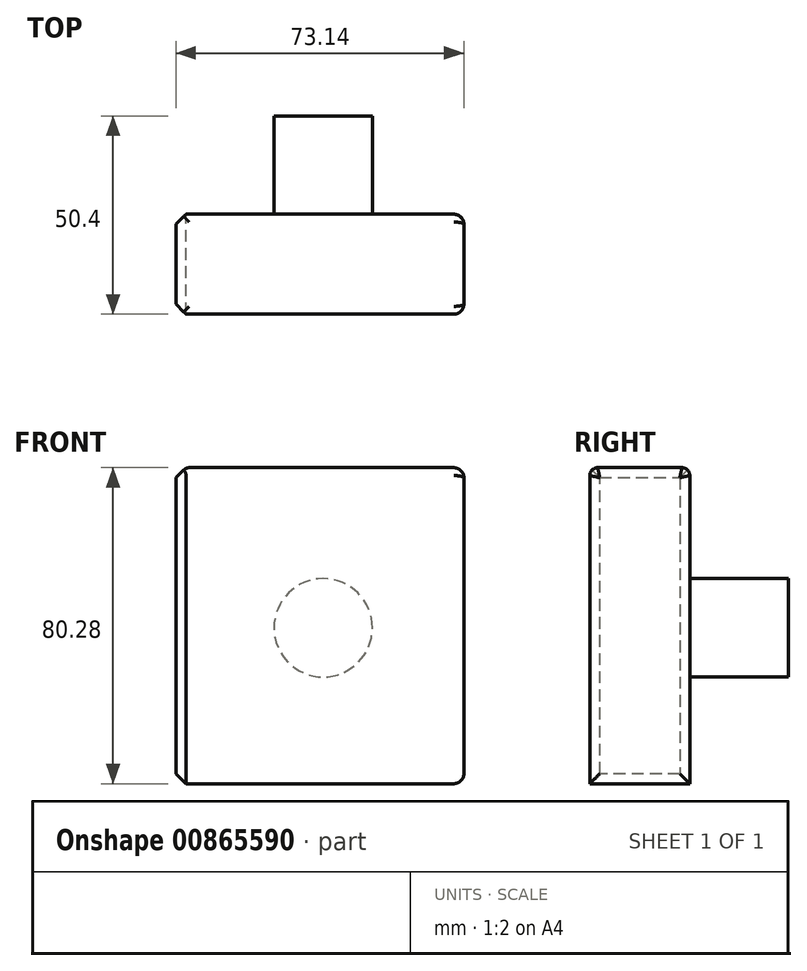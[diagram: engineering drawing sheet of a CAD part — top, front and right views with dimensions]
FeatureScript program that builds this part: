
annotation { "Feature Type Name" : "Feature", "Feature Type Description" : "" }
export const myFeature = defineFeature(function(context is Context, id is Id, definition is map)
    precondition{}
    {
        {
            var Q0;
            Q0=qCreatedBy(makeId("Front.planeOp"),FACE);
            var sketch = newSketch(context, id + "F0", { "sketchPlane" : qUnion([Q0])});
            skLineSegment(sketch, "E0.bottom", {"start": v(-37.4, 40.7) * mm, "end": v(35.75, 40.7) * mm});
            skLineSegment(sketch, "E0.top", {"start": v(-37.4, -39.6) * mm, "end": v(35.75, -39.6) * mm});
            skLineSegment(sketch, "E0.left", {"start": v(-37.4, 40.7) * mm, "end": v(-37.4, -39.6) * mm});
            skLineSegment(sketch, "E0.right", {"start": v(35.75, 40.7) * mm, "end": v(35.75, -39.6) * mm});
            skSolve(sketch);
        }
        {
            var Q0;
            Q0=makeQuery(id+"F0.imprint","IMPRINT",FACE,{"disambiguationData":[TD([[makeQuery(id+"F0.imprint","IMPRINT",EDGE,{"derivedFrom":sQuery(id+"F0.wireOp",EDGE,"E0.bottom")}),-1.0]])]});
            extrude(context, id + "F1", {"entities" : qUnion([Q0]), "depth" : 25.4 * mm, "offsetDistance" : 25.4 * mm});
        }
        {
            var Q0;
            Q0=qCreatedBy(makeId("Front.planeOp"),FACE);
            var sketch = newSketch(context, id + "F2", { "sketchPlane" : qUnion([Q0])});
            skCircle(sketch, "E1", {"center": v(0, 0) * mm, "radius": 12.5 * mm});
            skSolve(sketch);
        }
        {
            var Q0;
            Q0=makeQuery(id+"F1.opExtrude","SWEPT_FACE",FACE,{"disambiguationData":[OSD([sQuery(id+"F0.wireOp",EDGE,"E0.right")])]});
            fillet(context, id + "F3", {"entities" : qUnion([Q0]), "radius" : 2.54 * mm, "tangentPropagation" : true, "allowEdgeOverflow" : false});
        }
        {
            var Q0;
            Q0=makeQuery(id+"F1.opExtrude","SWEPT_FACE",FACE,{"disambiguationData":[OSD([sQuery(id+"F0.wireOp",EDGE,"E0.left")])]});
            chamfer(context, id + "F4", {"entities" : qUnion([Q0]), "width" : 2.54 * mm, "tangentPropagation" : true});
        }
        {
            var Q0;
            Q0=makeQuery(id+"F1.opExtrude","SWEPT_FACE",FACE,{"disambiguationData":[OSD([sQuery(id+"F0.wireOp",EDGE,"E0.bottom")])]});
            fillet(context, id + "F5", {"entities" : qUnion([Q0]), "radius" : 2 * mm, "tangentPropagation" : true, "allowEdgeOverflow" : false});
        }
        {
            var Q0;
            Q0=makeQuery(id+"F2.imprint","IMPRINT",FACE,{"disambiguationData":[TD([[makeQuery(id+"F2.imprint","IMPRINT",EDGE,{"derivedFrom":sQuery(id+"F2.wireOp",EDGE,"E1")}),1.0]])]});
            var Q1;
            Q1=sQuery(id+"F2.wireOp",EDGE,"E1");
            extrude(context, id + "F6", {"entities" : qUnion([Q0]), "surfaceEntities" : qUnion([Q1]), "oppositeDirection" : true, "depth" : 25 * mm, "offsetDistance" : 25 * mm});
        }
    });
